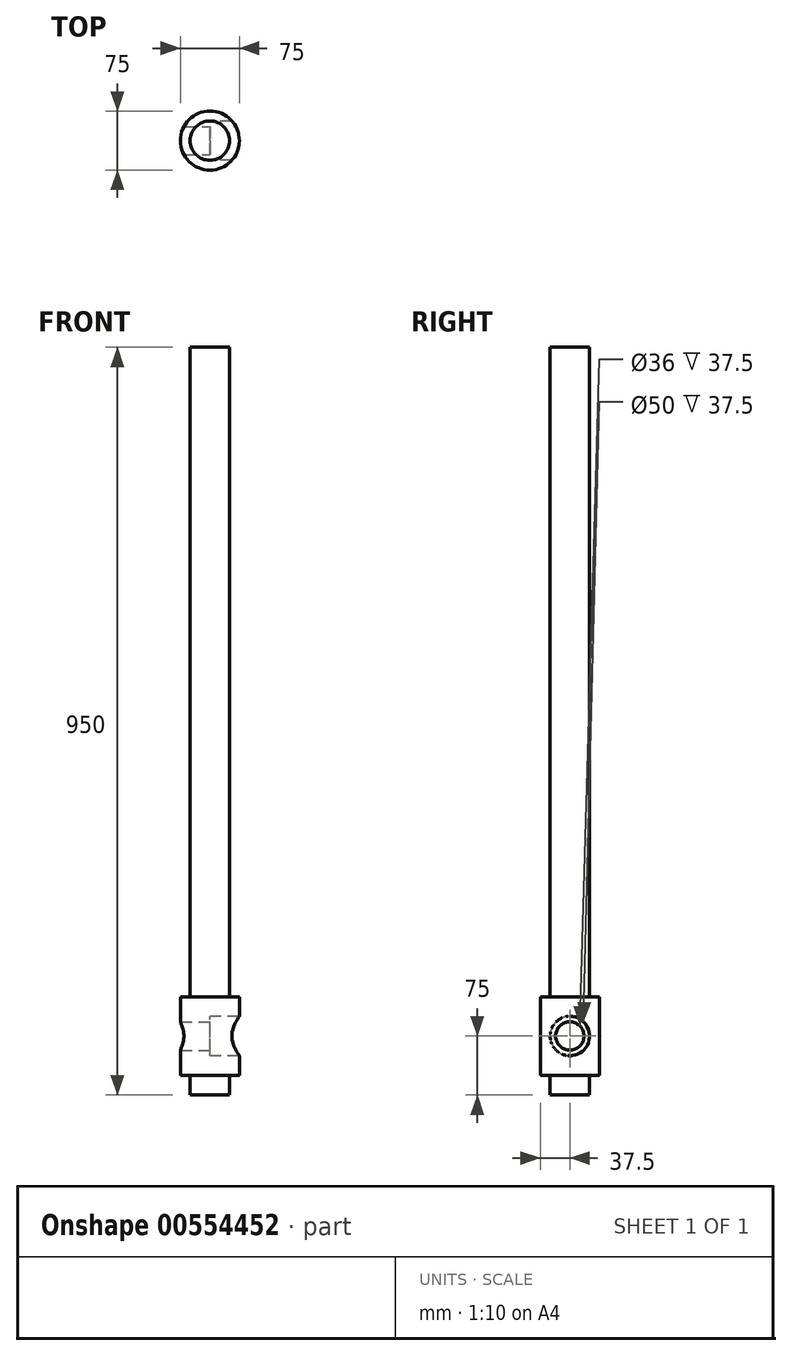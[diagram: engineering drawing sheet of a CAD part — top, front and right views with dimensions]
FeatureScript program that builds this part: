
annotation { "Feature Type Name" : "Feature", "Feature Type Description" : "" }
export const myFeature = defineFeature(function(context is Context, id is Id, definition is map)
    precondition{}
    {
        {
            var Q0;
            Q0=qCreatedBy(makeId("Top.planeOp"),FACE);
            var sketch = newSketch(context, id + "F0", { "sketchPlane" : qUnion([Q0])});
            skCircle(sketch, "E0", {"center": v(0, 0) * mm, "radius": 25 * mm});
            skCircle(sketch, "E1", {"center": v(0, 0) * mm, "radius": 37.5 * mm});
            skSolve(sketch);
        }
        {
            var Q0;
            Q0=makeQuery(id+"F0.imprint","IMPRINT",FACE,{"disambiguationData":[TD([[makeQuery(id+"F0.imprint","IMPRINT",EDGE,{"derivedFrom":sQuery(id+"F0.wireOp",EDGE,"E0")}),1.0]])]});
            extrude(context, id + "F1", {"entities" : qUnion([Q0]), "endBound" : BoundingType.SYMMETRIC, "depth" : 150 * mm, "offsetDistance" : 25 * mm});
        }
        {
            var Q0;
            Q0 = qSketchRegion(id + "F0", true);
            extrude(context, id + "F2", {"entities" : qUnion([Q0]), "operationType" : NewBodyOperationType.ADD, "endBound" : BoundingType.SYMMETRIC, "depth" : 100 * mm, "offsetDistance" : 25 * mm});
        }
        {
            var Q0;
            Q0=qCreatedBy(makeId("Right.planeOp"),FACE);
            var sketch = newSketch(context, id + "F3", { "sketchPlane" : qUnion([Q0])});
            skCircle(sketch, "E2", {"center": v(0, 0) * mm, "radius": 18 * mm});
            skSolve(sketch);
        }
        {
            var Q0;
            Q0 = qSketchRegion(id + "F3", true);
            extrude(context, id + "F4", {"entities" : qUnion([Q0]), "operationType" : NewBodyOperationType.REMOVE, "endBound" : BoundingType.THROUGH_ALL, "oppositeDirection" : true, "depth" : 35 * mm, "offsetDistance" : 25 * mm});
        }
        {
            var Q0;
            Q0=qCreatedBy(makeId("Right.planeOp"),FACE);
            var sketch = newSketch(context, id + "F5", { "sketchPlane" : qUnion([Q0])});
            skCircle(sketch, "E3", {"center": v(0, 0) * mm, "radius": 25 * mm});
            skSolve(sketch);
        }
        {
            var Q0;
            Q0 = qSketchRegion(id + "F5", true);
            extrude(context, id + "F6", {"entities" : qUnion([Q0]), "operationType" : NewBodyOperationType.REMOVE, "endBound" : BoundingType.THROUGH_ALL, "depth" : 25 * mm, "offsetDistance" : 25 * mm});
        }
        {
            var Q0;
            Q0=makeQuery(id+"F1.opExtrude","CAP_FACE",FACE,{"disambiguationData":[OSD([sQuery(id+"F0.wireOp",EDGE,"E0")])],"isStart":false});
            var sketch = newSketch(context, id + "F7", { "sketchPlane" : qUnion([Q0])});
            skCircle(sketch, "E4", {"center": v(0, 0) * mm, "radius": 25 * mm});
            skSolve(sketch);
        }
        {
            var Q0;
            Q0=makeQuery(id+"F7.imprint","IMPRINT",FACE,{"disambiguationData":[TD([[makeQuery(id+"F7.imprint","IMPRINT",EDGE,{"derivedFrom":sQuery(id+"F7.wireOp",EDGE,"E4")}),1.0]])]});
            extrude(context, id + "F8", {"entities" : qUnion([Q0]), "operationType" : NewBodyOperationType.ADD, "depth" : 800 * mm, "offsetDistance" : 25 * mm});
        }
    });
